# Revit family: CABINET1DR
name_source: partatom
category: Generic Models
revit_build: Autodesk Revit Architecture 2014 (Build: 20130308_1515(x64)
units: mm (PartAtom-declared; Revit-internal decimal feet)

## types (2) — shared parameters
InteriorCab1 = InteriorCab1
depth = 622 mm  [stored 2.04068 ft]
depth_gbl = 600 mm
door_code = 603 mm
gap_btm = 2 mm  [stored 0.00656168 ft]
gap_door = 3 mm  [stored 0.00984252 ft]
gap_left = 2 mm  [stored 0.00656168 ft]
gap_right = 2 mm  [stored 0.00656168 ft]
gap_top = 5 mm  [stored 0.0164042 ft]
height = 748 mm  [stored 2.45407 ft]
kick = 134 mm  [stored 0.439633 ft]
rails = 460 mm
thickness_back_material = 16 mm  [stored 0.0524934 ft]
thickness_door = 19 mm  [stored 0.062336 ft]
thickness_material = 19 mm  [stored 0.062336 ft]
thickness_material_minus = -19 mm  [stored -0.062336 ft]

## per-type parameters (varying)
| type | Exterior1 | width |
| config 2 | Exterior2 | 1200 mm |
| config 1 | Exterior1 | 900 mm  [stored 2.95276 ft] |

note: [stored X ft] marks values corroborated as IEEE doubles in the binary element streams (Revit-internal decimal feet)

## geometry (parser evidence)
native form markers: Sweep x4
no freeform markers — native parametric forms only
